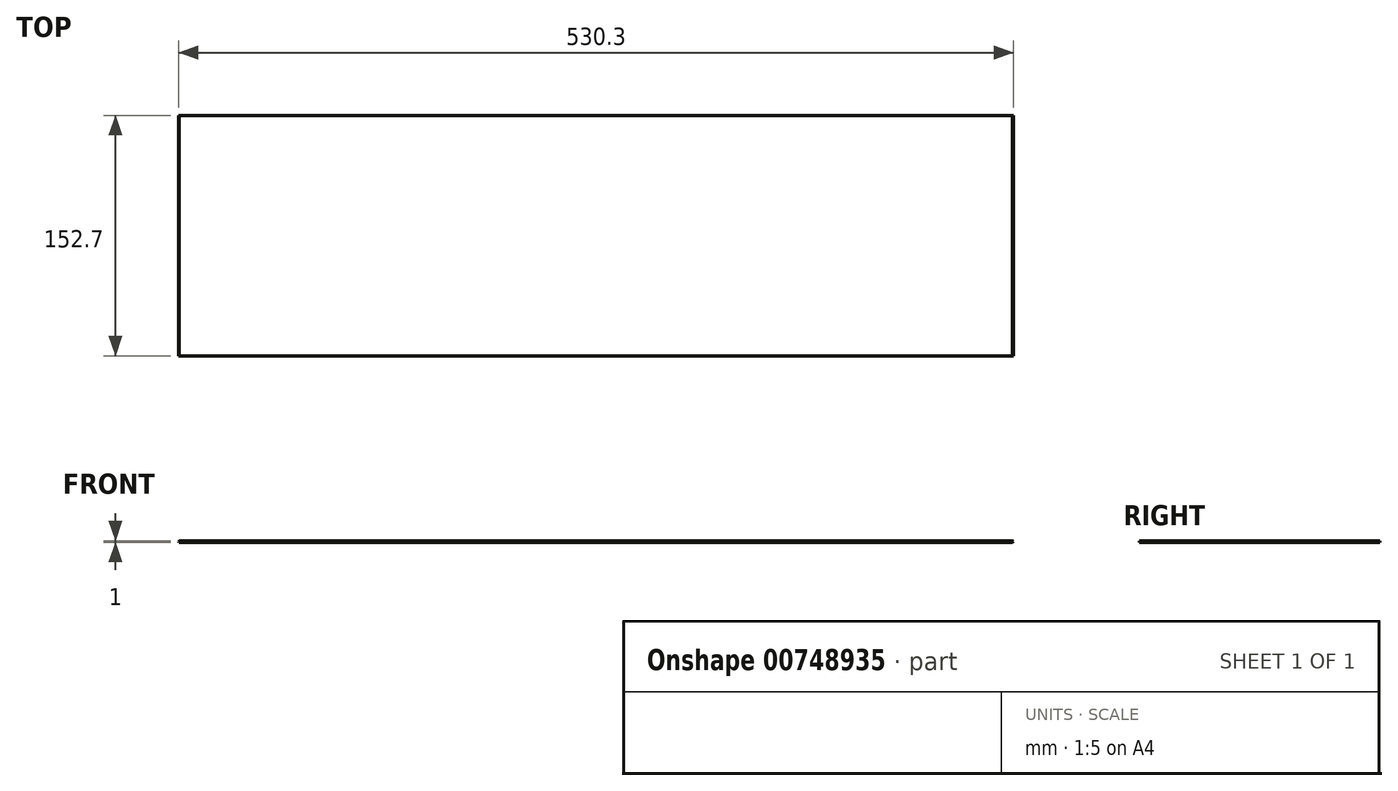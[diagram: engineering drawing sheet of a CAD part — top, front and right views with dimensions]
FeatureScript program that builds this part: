
annotation { "Feature Type Name" : "Feature", "Feature Type Description" : "" }
export const myFeature = defineFeature(function(context is Context, id is Id, definition is map)
    precondition{}
    {
        {
            var Q0;
            Q0=qCreatedBy(makeId("Front.planeOp"),FACE);
            var sketch = newSketch(context, id + "F0", { "sketchPlane" : qUnion([Q0])});
            skLineSegment(sketch, "E0.top", {"start": v(-262.23, -6.4) * mm, "end": v(267.07, -6.4) * mm});
            skPoint(sketch, "E0.middle", {"position": v(0, 0) * mm});
            skLineSegment(sketch, "E1", {"start": v(2.42, -1.06) * mm, "end": v(2.42, -0.39) * mm});
            skLineSegment(sketch, "E2.0", {"start": v(-262.23, -5.4) * mm, "end": v(267.07, -5.4) * mm});
            skPoint(sketch, "E3.start.orphan", {"position": v(272.87, -11.7) * mm});
            skLineSegment(sketch, "E4", {"start": v(-262.73, -5.9) * mm, "end": v(-262.23, -5.4) * mm});
            skLineSegment(sketch, "E5", {"start": v(-262.73, -5.9) * mm, "end": v(-262.23, -6.4) * mm});
            skLineSegment(sketch, "E6", {"start": v(267.57, -5.9) * mm, "end": v(267.07, -5.4) * mm});
            skLineSegment(sketch, "E7", {"start": v(267.57, -5.9) * mm, "end": v(267.07, -6.4) * mm});
            skPoint(sketch, "E8.orphan", {"position": v(267.57, -5.4) * mm});
            skPoint(sketch, "E9.orphan", {"position": v(267.57, -6.4) * mm});
            skPoint(sketch, "E10.orphan", {"position": v(-262.73, -6.4) * mm});
            skPoint(sketch, "E11.orphan", {"position": v(-262.73, -5.4) * mm});
            skSolve(sketch);
        }
        {
            var Q0;
            Q0 = qSketchRegion(id + "F0", true);
            extrude(context, id + "F1", {"entities" : qUnion([Q0]), "depth" : 152.7 * mm, "offsetDistance" : 25 * mm, "symmetric" : true});
        }
    });
